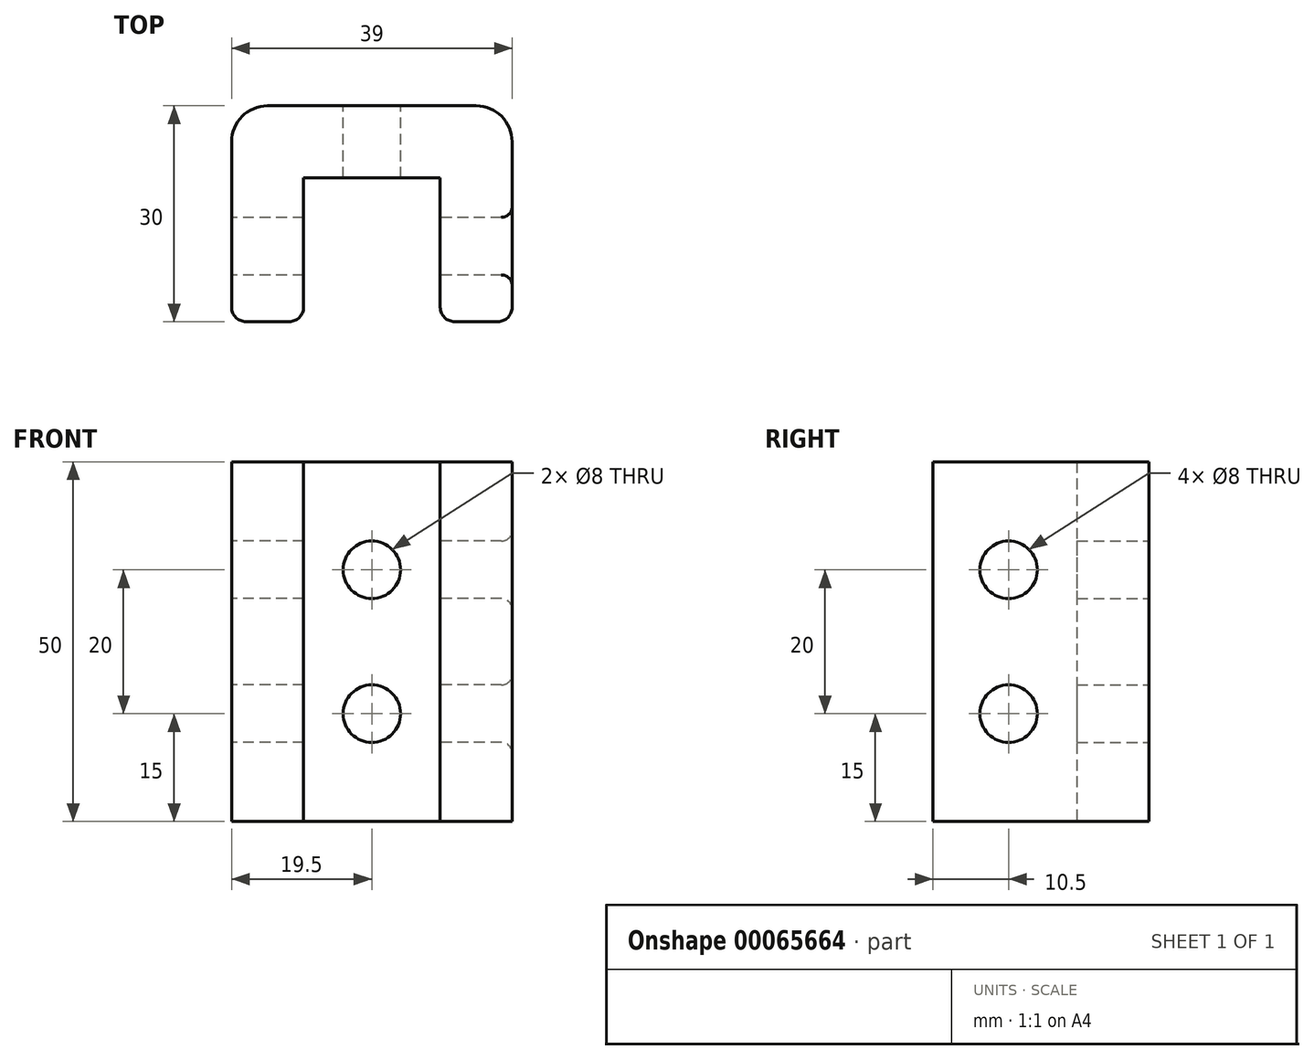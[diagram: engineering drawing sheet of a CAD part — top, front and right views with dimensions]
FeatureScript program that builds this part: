
annotation { "Feature Type Name" : "Feature", "Feature Type Description" : "" }
export const myFeature = defineFeature(function(context is Context, id is Id, definition is map)
    precondition{}
    {
        {
            var Q0;
            Q0=qCreatedBy(makeId("Top.planeOp"),FACE);
            var sketch = newSketch(context, id + "F0", { "sketchPlane" : qUnion([Q0])});
            skLineSegment(sketch, "E0.rect.bottom", {"start": v(-19.5, 15) * mm, "end": v(19.5, 15) * mm});
            skLineSegment(sketch, "E0.rect.top", {"start": v(-19.5, -15) * mm, "end": v(19.5, -15) * mm});
            skLineSegment(sketch, "E0.rect.left", {"start": v(-19.5, 15) * mm, "end": v(-19.5, -15) * mm});
            skLineSegment(sketch, "E0.rect.right", {"start": v(19.5, 15) * mm, "end": v(19.5, -15) * mm});
            skPoint(sketch, "E0.rect.middle", {"position": v(0, 0) * mm});
            skLineSegment(sketch, "E1.bottom", {"start": v(-9.5, -15) * mm, "end": v(9.5, -15) * mm});
            skLineSegment(sketch, "E1.top", {"start": v(-9.5, 5) * mm, "end": v(9.5, 5) * mm});
            skLineSegment(sketch, "E1.left", {"start": v(-9.5, -15) * mm, "end": v(-9.5, 5) * mm});
            skLineSegment(sketch, "E1.right", {"start": v(9.5, -15) * mm, "end": v(9.5, 5) * mm});
            skPoint(sketch, "E2", {"position": v(0, 5) * mm});
            skSolve(sketch);
        }
        {
            var Q0;
            Q0=makeQuery(id+"F0.imprint","IMPRINT",FACE,{"disambiguationData":[TD([[makeQuery(id+"F0.imprint","IMPRINT",EDGE,{"derivedFrom":sQuery(id+"F0.wireOp",EDGE,"E0.rect.bottom")}),-1.0]])]});
            var Q1;
            Q1=makeQuery(id+"F0.imprint","IMPRINT",FACE,{"disambiguationData":[TD([[makeQuery(id+"F0.imprint","IMPRINT",EDGE,{"derivedFrom":sQuery(id+"F0.wireOp",EDGE,"E1.bottom")}),1.0]])]});
            extrude(context, id + "F1", {"entities" : qUnion([Q0, Q1]), "depth" : 5 * mm});
        }
        {
            var Q0;
            Q0=makeQuery(id+"F0.imprint","IMPRINT",FACE,{"disambiguationData":[TD([[makeQuery(id+"F0.imprint","IMPRINT",EDGE,{"derivedFrom":sQuery(id+"F0.wireOp",EDGE,"E0.rect.bottom")}),-1.0]])]});
            extrude(context, id + "F2", {"entities" : qUnion([Q0]), "operationType" : NewBodyOperationType.ADD, "depth" : 50 * mm});
        }
        {
            var Q0;
            {var subQ0=sQuery(id+"F0.wireOp",EDGE,"E0.rect.left");Q0=makeQuery(id+"F2.boolean.opBoolean","MERGE",FACE,{"derivedFrom":[makeQuery(id+"F1.opExtrude","SWEPT_FACE",FACE,{"disambiguationData":[OSD([subQ0])]}),makeQuery(id+"F2.opExtrude","SWEPT_FACE",FACE,{"disambiguationData":[OSD([subQ0])]})]});}
            var sketch = newSketch(context, id + "F3", { "sketchPlane" : qUnion([Q0])});
            skPoint(sketch, "E3", {"position": v(4.5, 15) * mm});
            skPoint(sketch, "E4", {"position": v(4.5, 35) * mm});
            skCircle(sketch, "E5", {"center": v(4.5, 15) * mm, "radius": 4 * mm});
            skCircle(sketch, "E6", {"center": v(4.5, 35) * mm, "radius": 4 * mm});
            skSolve(sketch);
        }
        {
            var Q0;
            Q0=makeQuery(id+"F3.imprint","IMPRINT",FACE,{"disambiguationData":[TD([[makeQuery(id+"F3.imprint","IMPRINT",EDGE,{"derivedFrom":sQuery(id+"F3.wireOp",EDGE,"E5")}),1.0]])]});
            var Q1;
            Q1=makeQuery(id+"F3.imprint","IMPRINT",FACE,{"disambiguationData":[TD([[makeQuery(id+"F3.imprint","IMPRINT",EDGE,{"derivedFrom":sQuery(id+"F3.wireOp",EDGE,"E6")}),1.0]])]});
            extrude(context, id + "F4", {"entities" : qUnion([Q0, Q1]), "operationType" : NewBodyOperationType.REMOVE, "oppositeDirection" : true, "depth" : 40 * mm});
        }
        {
            var Q0;
            {var subQ0=sQuery(id+"F0.wireOp",EDGE,"E0.rect.bottom");Q0=makeQuery(id+"F2.boolean.opBoolean","MERGE",FACE,{"derivedFrom":[makeQuery(id+"F1.opExtrude","SWEPT_FACE",FACE,{"disambiguationData":[OSD([subQ0])]}),makeQuery(id+"F2.opExtrude","SWEPT_FACE",FACE,{"disambiguationData":[OSD([subQ0])]})]});}
            var sketch = newSketch(context, id + "F5", { "sketchPlane" : qUnion([Q0])});
            skPoint(sketch, "E7", {"position": v(0, 15) * mm});
            skPoint(sketch, "E8", {"position": v(0, 35) * mm});
            skCircle(sketch, "E9", {"center": v(0, 15) * mm, "radius": 4 * mm});
            skCircle(sketch, "E10", {"center": v(0, 35) * mm, "radius": 4 * mm});
            skSolve(sketch);
        }
        {
            var Q0;
            Q0=makeQuery(id+"F5.imprint","IMPRINT",FACE,{"disambiguationData":[TD([[makeQuery(id+"F5.imprint","IMPRINT",EDGE,{"derivedFrom":sQuery(id+"F5.wireOp",EDGE,"E9")}),1.0]])]});
            var Q1;
            Q1=makeQuery(id+"F5.imprint","IMPRINT",FACE,{"disambiguationData":[TD([[makeQuery(id+"F5.imprint","IMPRINT",EDGE,{"derivedFrom":sQuery(id+"F5.wireOp",EDGE,"E10")}),1.0]])]});
            extrude(context, id + "F6", {"entities" : qUnion([Q0, Q1]), "operationType" : NewBodyOperationType.REMOVE, "oppositeDirection" : true, "depth" : 10 * mm});
        }
        {
            var Q0;
            Q0=makeQuery(id+"F4.boolean.opBoolean","COPY",EDGE,{"derivedFrom":makeQuery(id+"F4.opExtrude","CAP_EDGE",EDGE,{"disambiguationData":[OSD([sQuery(id+"F3.wireOp",EDGE,"E5")])],"isStart":true})});
            var Q1;
            Q1=makeQuery(id+"F4.boolean.opBoolean","COPY",EDGE,{"derivedFrom":makeQuery(id+"F4.opExtrude","CAP_EDGE",EDGE,{"disambiguationData":[OSD([sQuery(id+"F3.wireOp",EDGE,"E6")])],"isStart":true})});
            var Q2;
            Q2=makeQuery(id+"F6.boolean.opBoolean","COPY",EDGE,{"derivedFrom":makeQuery(id+"F6.opExtrude","CAP_EDGE",EDGE,{"disambiguationData":[OSD([sQuery(id+"F5.wireOp",EDGE,"E10")])],"isStart":true})});
            var Q3;
            Q3=makeQuery(id+"F6.boolean.opBoolean","COPY",EDGE,{"derivedFrom":makeQuery(id+"F6.opExtrude","CAP_EDGE",EDGE,{"disambiguationData":[OSD([sQuery(id+"F5.wireOp",EDGE,"E9")])],"isStart":true})});
            var Q4;
            {var subQ0=sQuery(id+"F0.wireOp",EDGE,"E0.rect.right");Q4=makeQuery(id+"F4.boolean.opBoolean","INTERSECT",EDGE,{"derivedFrom":[makeQuery(id+"F2.boolean.opBoolean","MERGE",FACE,{"derivedFrom":[makeQuery(id+"F1.opExtrude","SWEPT_FACE",FACE,{"disambiguationData":[OSD([subQ0])]}),makeQuery(id+"F2.opExtrude","SWEPT_FACE",FACE,{"disambiguationData":[OSD([subQ0])]})]}),makeQuery(id+"F4.opExtrude","SWEPT_FACE",FACE,{"disambiguationData":[OSD([sQuery(id+"F3.wireOp",EDGE,"E6")])]})]});}
            var Q5;
            {var subQ0=sQuery(id+"F0.wireOp",EDGE,"E0.rect.right");Q5=makeQuery(id+"F4.boolean.opBoolean","INTERSECT",EDGE,{"derivedFrom":[makeQuery(id+"F2.boolean.opBoolean","MERGE",FACE,{"derivedFrom":[makeQuery(id+"F1.opExtrude","SWEPT_FACE",FACE,{"disambiguationData":[OSD([subQ0])]}),makeQuery(id+"F2.opExtrude","SWEPT_FACE",FACE,{"disambiguationData":[OSD([subQ0])]})]}),makeQuery(id+"F4.opExtrude","SWEPT_FACE",FACE,{"disambiguationData":[OSD([sQuery(id+"F3.wireOp",EDGE,"E5")])]})]});}
            fillet(context, id + "F7", {"entities" : qUnion([Q0, Q1, Q2, Q3, Q4, Q5]), "radius" : 1.5 * mm, "tangentPropagation" : true, "allowEdgeOverflow" : false});
        }
        {
            var Q0;
            Q0=makeQuery(id+"F1.opExtrude","CAP_FACE",FACE,{"disambiguationData":[OSD([sQuery(id+"F0.wireOp",EDGE,"E0.rect.bottom"),sQuery(id+"F0.wireOp",EDGE,"E0.rect.top"),sQuery(id+"F0.wireOp",EDGE,"E0.rect.left"),sQuery(id+"F0.wireOp",EDGE,"E0.rect.right"),sQuery(id+"F0.wireOp",EDGE,"E1.bottom")])],"isStart":true});
            var sketch = newSketch(context, id + "F8", { "sketchPlane" : qUnion([Q0])});
            skText(sketch, "E11", { "text": "19", "fontName": "Arimo-Bold.ttf"});
            skPoint(sketch, "E12", {"position": v(0, 0) * mm});
            const initialGuessF8  = {"E11": [0.00604, 0.00404, -1, 0, 0.00809]};
            skSetInitialGuess(sketch, initialGuessF8);
            skSolve(sketch);
        }
        {
            var Q0;
            Q0 = qSketchRegion(id + "F8", true);
            extrude(context, id + "F9", {"entities" : qUnion([Q0]), "operationType" : NewBodyOperationType.REMOVE, "oppositeDirection" : true, "depth" : 5 * mm});
        }
        {
            var Q0;
            {var subQ0=sQuery(id+"F0.wireOp",EDGE,"E0.rect.right");var subQ1=sQuery(id+"F0.wireOp",EDGE,"E0.rect.bottom");Q0=makeQuery(id+"F2.boolean.opBoolean","MERGE",EDGE,{"derivedFrom":[makeQuery(id+"F1.opExtrude","SWEPT_EDGE",EDGE,{"disambiguationData":[OSD([subQ1,subQ0])]}),makeQuery(id+"F2.opExtrude","SWEPT_EDGE",EDGE,{"disambiguationData":[OSD([subQ1,subQ0])]})]});}
            var Q1;
            {var subQ0=sQuery(id+"F0.wireOp",EDGE,"E0.rect.left");var subQ1=sQuery(id+"F0.wireOp",EDGE,"E0.rect.bottom");Q1=makeQuery(id+"F2.boolean.opBoolean","MERGE",EDGE,{"derivedFrom":[makeQuery(id+"F1.opExtrude","SWEPT_EDGE",EDGE,{"disambiguationData":[OSD([subQ1,subQ0])]}),makeQuery(id+"F2.opExtrude","SWEPT_EDGE",EDGE,{"disambiguationData":[OSD([subQ1,subQ0])]})]});}
            fillet(context, id + "F10", {"entities" : qUnion([Q0, Q1]), "radius" : 5 * mm, "tangentPropagation" : true, "allowEdgeOverflow" : false});
        }
        {
            var Q0;
            Q0=makeQuery(id+"F2.opExtrude","SWEPT_EDGE",EDGE,{"disambiguationData":[OSD([sQuery(id+"F0.wireOp",EDGE,"E0.rect.top"),sQuery(id+"F0.wireOp",EDGE,"E1.bottom"),sQuery(id+"F0.wireOp",EDGE,"E1.left")])]});
            var Q1;
            Q1=makeQuery(id+"F2.opExtrude","SWEPT_EDGE",EDGE,{"disambiguationData":[OSD([sQuery(id+"F0.wireOp",EDGE,"E0.rect.top"),sQuery(id+"F0.wireOp",EDGE,"E1.bottom"),sQuery(id+"F0.wireOp",EDGE,"E1.right")])]});
            var Q2;
            {var subQ0=sQuery(id+"F0.wireOp",EDGE,"E0.rect.right");var subQ1=sQuery(id+"F0.wireOp",EDGE,"E0.rect.top");Q2=makeQuery(id+"F2.boolean.opBoolean","MERGE",EDGE,{"derivedFrom":[makeQuery(id+"F1.opExtrude","SWEPT_EDGE",EDGE,{"disambiguationData":[OSD([subQ1,subQ0])]}),makeQuery(id+"F2.opExtrude","SWEPT_EDGE",EDGE,{"disambiguationData":[OSD([subQ1,subQ0])]})]});}
            var Q3;
            {var subQ0=sQuery(id+"F0.wireOp",EDGE,"E0.rect.left");var subQ1=sQuery(id+"F0.wireOp",EDGE,"E0.rect.top");Q3=makeQuery(id+"F2.boolean.opBoolean","MERGE",EDGE,{"derivedFrom":[makeQuery(id+"F1.opExtrude","SWEPT_EDGE",EDGE,{"disambiguationData":[OSD([subQ1,subQ0])]}),makeQuery(id+"F2.opExtrude","SWEPT_EDGE",EDGE,{"disambiguationData":[OSD([subQ1,subQ0])]})]});}
            fillet(context, id + "F11", {"entities" : qUnion([Q0, Q1, Q2, Q3]), "radius" : 2 * mm, "tangentPropagation" : true, "allowEdgeOverflow" : false});
        }
    });
